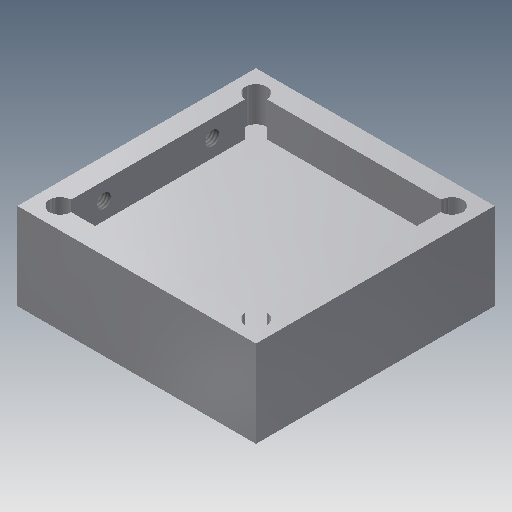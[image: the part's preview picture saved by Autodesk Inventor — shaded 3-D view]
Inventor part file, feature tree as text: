
AUTODESK INVENTOR PART (.ipt)
format: ipt  version: 2019 (Build 230136000, 136)  size: 162,816 bytes
history: native  units: mm
features: sketch x7, hole x4, extrude x3, projected_geometry x3
ambient origin geometry x8: Origin, YZ Plane, XZ Plane, XY Plane, X Axis, Y Axis, Z Axis, Center Point
bodies: Solid1 (feature_tree)
feature tree (17):
  extrude  "Extrusion1"  Depth=55.0mm
  hole  "Hole2"  [1 undecoded]
  extrude  "Extrusion3"  Depth=8.0mm TaperAngle=0.0deg
  hole  "Hole3"  [1 undecoded]
  extrude  "Extrusion4"  Depth=25.0mm
  hole  "Hole5"  [1 undecoded]
  hole  "Hole6"  [1 undecoded]
  sketch  "Sketch1"  dims[d0=55.0mm d1=55.0mm]
  sketch  "Sketch4"  dims[d2=20.0mm d3=0.0mm d15=45.1mm]
  sketch  "Sketch5"  dims[d16=45.1mm]
  sketch  "Sketch6"  dims[d17=5.0mm d18=6.0mm d19=4.0mm d20=2.0mm d21=90.0deg d22=8.0mm d23=0.0mm d24=8.0mm d25=0.0mm]
  projected_geometry  "Projected Loop1"
  sketch  "Sketch8"  dims[d26=15.0mm d27=15.0mm]
  projected_geometry  "Projected Loop2"
  sketch  "Sketch9"  dims[d28=3.242mm d29=6.0mm d30=4.0mm d31=2.0mm d32=90.0deg d33=8.0mm d34=20.594885mm d44=25.0mm]
  projected_geometry  "Projected Loop3"
  sketch  "Sketch10"  dims[d45=25.0mm d46=6.0mm d47=0.0mm d48=3.0mm d49=6.0mm d50=4.0mm d51=2.0mm d52=90.0deg d53=6.0mm d54=0.0mm d55=3.242mm d56=8.0mm d57=4.0mm d58=2.0mm d59=90.0deg d60=4.0mm d61=20.594885mm]
note: 4 required parameter values undecoded (feature->parameter linkage not recoverable at this tier; creation-order binding heuristic only, values carry confidence <= 0.55)
